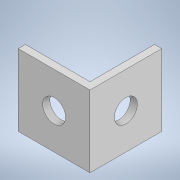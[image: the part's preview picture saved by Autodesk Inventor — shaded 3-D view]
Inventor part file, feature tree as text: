
AUTODESK INVENTOR PART (.ipt)
format: ipt  version: 2021 (Build 250183000, 183)  size: 114,176 bytes
history: native  units: mm
features: sketch x3, hole x2, extrude x1
ambient origin geometry x8: Origin, YZ Plane, XZ Plane, XY Plane, X Axis, Y Axis, Z Axis, Center Point
bodies: Solid1 (feature_tree)
feature tree (6):
  extrude  "Extrusion1"  Depth=10.0mm
  hole  "Hole1"  [1 undecoded]
  hole  "Hole2"  [1 undecoded]
  sketch  "Sketch1"  dims[d1=10.0mm d2=10.0mm]
  sketch  "Sketch2"  dims[d3=1.0mm d4=9.0mm]
  sketch  "Sketch3"  dims[d5=9.0mm d6=10.0mm d7=0.0mm d8=3.2mm d9=6.0mm d10=4.0mm d11=2.0mm d12=90.0deg d13=8.0mm d14=20.594885mm d15=3.2mm d16=6.0mm d17=4.0mm d18=2.0mm d19=90.0deg d20=8.0mm d21=20.594885mm]
note: 2 required parameter values undecoded (feature->parameter linkage not recoverable at this tier; creation-order binding heuristic only, values carry confidence <= 0.55)
